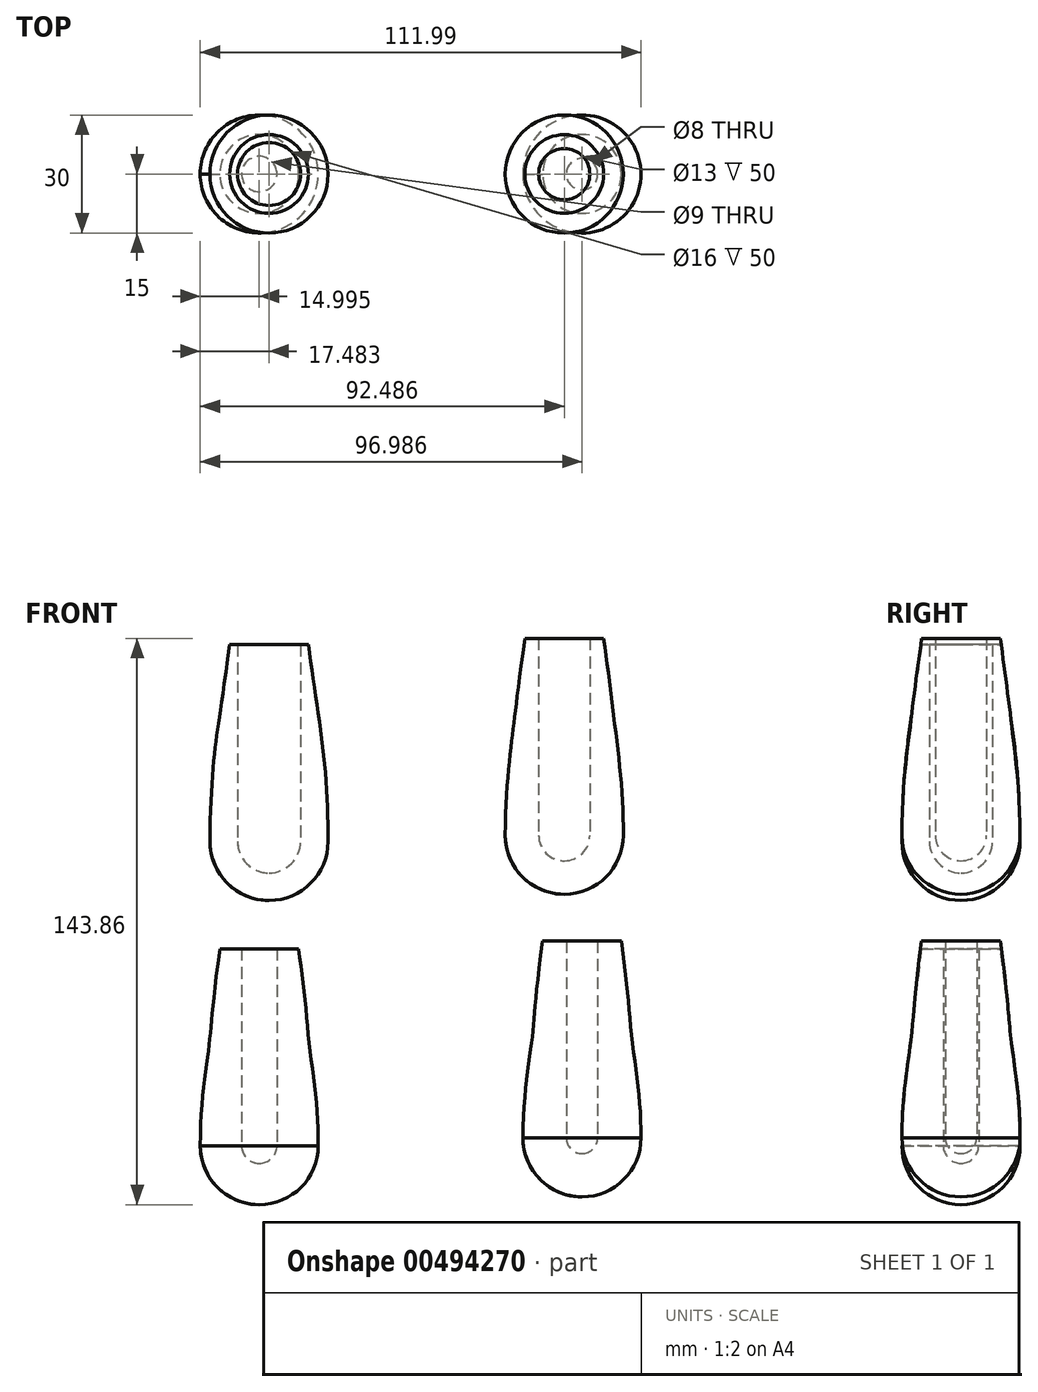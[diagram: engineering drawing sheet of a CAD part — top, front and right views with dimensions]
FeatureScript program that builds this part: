
annotation { "Feature Type Name" : "Feature", "Feature Type Description" : "" }
export const myFeature = defineFeature(function(context is Context, id is Id, definition is map)
    precondition{}
    {
        {
            var Q0;
            Q0=qCreatedBy(makeId("Front.planeOp"),FACE);
            var sketch = newSketch(context, id + "F0", { "sketchPlane" : qUnion([Q0])});
            skCircle(sketch, "E0", {"center": v(-41.5, 21.7) * mm, "radius": 15 * mm, "construction": true});
            skLineSegment(sketch, "E1", {"start": v(-49.5, 21.7) * mm, "end": v(-49.5, 71.7) * mm});
            skLineSegment(sketch, "E2", {"start": v(-49.5, 71.7) * mm, "end": v(-51.5, 71.7) * mm});
            skArc(sketch, "E3", {"start": v(-41.5, 6.7) * mm, "mid": v(-52.11, 11.1) * mm, "end": v(-56.5, 21.7) * mm});
            skFitSpline(sketch, "E4", {"points": [v(-56.5, 21.7) * mm, v(-55.11, 46.03) * mm, v(-51.5, 71.7) * mm], "startDerivative": vector(0, 64.62) * mm, "endDerivative": vector(12.44, 90.97) * mm});
            skLineSegment(sketch, "E5", {"start": v(-41.5, 21.7) * mm, "end": v(-49.5, 21.7) * mm, "construction": true});
            skLineSegment(sketch, "E6", {"start": v(-41.5, 6.7) * mm, "end": v(-41.5, 13.7) * mm});
            skLineSegment(sketch, "E7", {"start": v(-41.5, 13.7) * mm, "end": v(-41.5, 21.7) * mm, "construction": true});
            skArc(sketch, "E8", {"start": v(-49.5, 21.7) * mm, "mid": v(-47.16, 16.04) * mm, "end": v(-41.5, 13.7) * mm});
            skCircle(sketch, "E9", {"center": v(33.5, 23.27) * mm, "radius": 15 * mm, "construction": true});
            skLineSegment(sketch, "E10", {"start": v(27, 23.27) * mm, "end": v(27, 73.27) * mm});
            skLineSegment(sketch, "E11", {"start": v(27, 73.27) * mm, "end": v(23.5, 73.27) * mm});
            skArc(sketch, "E12", {"start": v(33.5, 8.27) * mm, "mid": v(22.89, 12.66) * mm, "end": v(18.5, 23.27) * mm});
            skFitSpline(sketch, "E13", {"points": [v(18.5, 23.27) * mm, v(20.22, 47.79) * mm, v(23.5, 73.27) * mm], "startDerivative": vector(0, 64.62) * mm, "endDerivative": vector(12.44, 90.97) * mm});
            skLineSegment(sketch, "E14", {"start": v(33.5, 23.27) * mm, "end": v(27, 23.27) * mm, "construction": true});
            skLineSegment(sketch, "E15", {"start": v(33.5, 8.27) * mm, "end": v(33.5, 16.77) * mm});
            skLineSegment(sketch, "E16", {"start": v(33.5, 16.77) * mm, "end": v(33.5, 23.27) * mm, "construction": true});
            skArc(sketch, "E17", {"start": v(27, 23.27) * mm, "mid": v(28.9, 18.68) * mm, "end": v(33.5, 16.77) * mm});
            skCircle(sketch, "E18", {"center": v(38, -53.6) * mm, "radius": 15 * mm, "construction": true});
            skLineSegment(sketch, "E19", {"start": v(34, -53.6) * mm, "end": v(34, -3.6) * mm});
            skLineSegment(sketch, "E20", {"start": v(34, -3.6) * mm, "end": v(28, -3.6) * mm});
            skArc(sketch, "E21", {"start": v(38, -68.6) * mm, "mid": v(27.39, -64.2) * mm, "end": v(23, -53.6) * mm});
            skFitSpline(sketch, "E22", {"points": [v(23, -53.6) * mm, v(25.28, -28.77) * mm, v(28, -3.6) * mm], "startDerivative": vector(0, 64.62) * mm, "endDerivative": vector(12.44, 90.97) * mm});
            skLineSegment(sketch, "E23", {"start": v(38, -53.6) * mm, "end": v(34, -53.6) * mm, "construction": true});
            skLineSegment(sketch, "E24", {"start": v(38, -68.6) * mm, "end": v(38, -57.6) * mm});
            skLineSegment(sketch, "E25", {"start": v(38, -57.6) * mm, "end": v(38, -53.6) * mm, "construction": true});
            skArc(sketch, "E26", {"start": v(34, -53.6) * mm, "mid": v(35.17, -56.43) * mm, "end": v(38, -57.6) * mm});
            skCircle(sketch, "E27", {"center": v(-44, -55.6) * mm, "radius": 15 * mm, "construction": true});
            skLineSegment(sketch, "E28", {"start": v(-48.5, -55.6) * mm, "end": v(-48.5, -5.6) * mm});
            skLineSegment(sketch, "E29", {"start": v(-48.5, -5.6) * mm, "end": v(-54, -5.6) * mm});
            skArc(sketch, "E30", {"start": v(-44, -70.6) * mm, "mid": v(-54.6, -66.2) * mm, "end": v(-59, -55.6) * mm});
            skFitSpline(sketch, "E31", {"points": [v(-59, -55.6) * mm, v(-56.82, -30.82) * mm, v(-54, -5.6) * mm], "startDerivative": vector(0, 64.62) * mm, "endDerivative": vector(12.44, 90.97) * mm});
            skLineSegment(sketch, "E32", {"start": v(-44, -55.6) * mm, "end": v(-48.5, -55.6) * mm, "construction": true});
            skLineSegment(sketch, "E33", {"start": v(-44, -70.6) * mm, "end": v(-44, -60.1) * mm});
            skLineSegment(sketch, "E34", {"start": v(-44, -60.1) * mm, "end": v(-44, -55.6) * mm, "construction": true});
            skArc(sketch, "E35", {"start": v(-48.5, -55.6) * mm, "mid": v(-47.18, -58.77) * mm, "end": v(-44, -60.1) * mm});
            skSolve(sketch);
        }
        {
            var Q0;
            Q0=makeQuery(id+"F0.imprint","IMPRINT",FACE,{"disambiguationData":[TD([[makeQuery(id+"F0.imprint","IMPRINT",EDGE,{"derivedFrom":sQuery(id+"F0.wireOp",EDGE,"E1")}),1.0]])]});
            var Q1;
            Q1=sQuery(id+"F0.wireOp",EDGE,"E6");
            revolve(context, id + "F1", {"entities" : qUnion([Q0]), "axis" : qUnion([Q1]), "revolveType" : RevolveType.FULL});
        }
        {
            var Q0;
            Q0=makeQuery(id+"F0.imprint","IMPRINT",FACE,{"disambiguationData":[TD([[makeQuery(id+"F0.imprint","IMPRINT",EDGE,{"derivedFrom":sQuery(id+"F0.wireOp",EDGE,"E10")}),1.0]])]});
            var Q1;
            Q1=sQuery(id+"F0.wireOp",EDGE,"E15");
            revolve(context, id + "F2", {"entities" : qUnion([Q0]), "axis" : qUnion([Q1]), "revolveType" : RevolveType.FULL});
        }
        {
            var Q0;
            Q0=makeQuery(id+"F0.imprint","IMPRINT",FACE,{"disambiguationData":[TD([[makeQuery(id+"F0.imprint","IMPRINT",EDGE,{"derivedFrom":sQuery(id+"F0.wireOp",EDGE,"E28")}),1.0]])]});
            var Q1;
            Q1=sQuery(id+"F0.wireOp",EDGE,"E33");
            revolve(context, id + "F3", {"entities" : qUnion([Q0]), "axis" : qUnion([Q1]), "revolveType" : RevolveType.FULL});
        }
        {
            var Q0;
            Q0=makeQuery(id+"F0.imprint","IMPRINT",FACE,{"disambiguationData":[TD([[makeQuery(id+"F0.imprint","IMPRINT",EDGE,{"derivedFrom":sQuery(id+"F0.wireOp",EDGE,"E19")}),1.0]])]});
            var Q1;
            Q1=sQuery(id+"F0.wireOp",EDGE,"E24");
            revolve(context, id + "F4", {"entities" : qUnion([Q0]), "axis" : qUnion([Q1]), "revolveType" : RevolveType.FULL});
        }
    });
